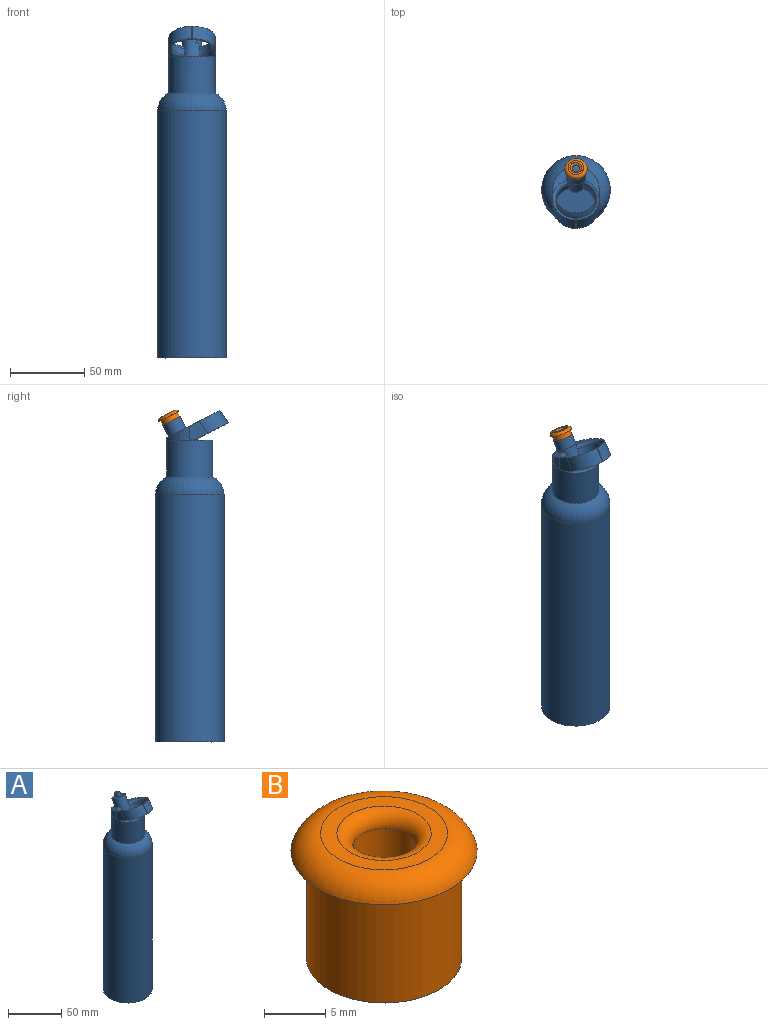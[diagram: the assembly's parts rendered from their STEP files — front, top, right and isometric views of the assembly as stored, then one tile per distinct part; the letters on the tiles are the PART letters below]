
ASSEMBLY  parts=2 mates=1
PART A: 28 faces, bbox 46.8x51.6x225.1 mm
  f0: plane 3.56x1.85mm, normal (0,-0.46,-0.89), area 3.1mm2, adj f2,f8,f24
  f1: plane 30.53x14.5mm, normal (0,-0.46,-0.89), area 25.3mm2, adj f6,f15,f20,f21,f24
  f2: plane 10.81x10.7mm, normal (0,-0.01,-1), area 81.4mm2, adj f0,f8,f10,f18,f22,f24
  f3: cylinder r=13.31mm len=26.62mm, axis (0,0.46,0.89), area 362.6mm2, adj f22,f24,f25
  f4: plane 2.04x1.94mm, normal (0,1,0), area 1.3mm2, adj f5,f9,f17,f19
  f5: plane 31.13x21.03mm, normal (0,0.46,0.89), area 178.6mm2, adj f4,f6,f8,f17,f18,f19,f22,f25
  f6: plane 13.61x12.89mm, normal (1,0,0), area 113.2mm2, adj f1,f5,f7,f14,f19,f21,f24,f25
  f7: plane 19.47x15.6mm, normal (0,-0.01,-1), area 85.2mm2, adj f6,f9,f10,f14,f19,f22,f24
  f8: plane 13.03x12.68mm, normal (-1,0,0), area 102.7mm2, adj f0,f2,f5,f18,f20,f24,f25
  f9: cylinder r=15.56mm len=31.12mm, axis (0,0,-1), area 2432mm2, adj f4,f7,f10,f13,f16,f17
  f10: plane 31.12x22.48mm, normal (0,0,1), area 496.2mm2, adj f2,f7,f9,f16,f22
  f11: cylinder r=22.99mm len=166.25mm, axis (0,0,-1), area 24011.4mm2, adj f12,f13
  f12: plane 45.97x45.97mm, normal (0,0,-1), area 1660mm2, adj f11
  f13: torus R=10.29mm, axis (0,0,1), area 1859.7mm2, adj f9,f11
  f14: plane 6.29x3.27mm, normal (0,-0.46,-0.89), area 6.1mm2, adj f6,f7,f24
  f15: plane 8.24x5.76mm, normal (0,-0.82,0.57), area 5.6mm2, adj f1,f20,f21,f25
  f16: plane 13.94x8.64mm, normal (0,0.01,1), area 0.7mm2, adj f9,f10,f17
  f17: cylinder r=15.58mm len=13.87mm, axis (0,-0.01,-1), area 50.5mm2, adj f4,f5,f9,f16,f18
  f18: extruded ~9.4x7.01mm, area 54.4mm2, adj f2,f5,f8,f17
  f19: cylinder r=15.48mm len=15.38mm, axis (0,-0.01,-1), area 94.5mm2, adj f4,f5,f6,f7
  f20: cylinder r=15.24mm len=19.38mm, axis (0,-0.57,-0.82), area 243.3mm2, adj f1,f8,f15,f24,f25
  f21: cylinder r=15.24mm len=19.42mm, axis (0,0.57,0.82), area 241mm2, adj f1,f6,f15,f25
  f22: cylinder r=6.59mm len=21.88mm, axis (0,-0.46,-0.89), area 457.8mm2, adj f2,f3,f5,f7,f10,f23,f24,f25
  f23: plane 13.17x11.69mm, normal (0,0.46,0.89), area 116mm2, adj f22,f26
  f24: torus R=15.85mm, axis (0,-0.46,-0.89), area 266.9mm2, adj f0,f1,f2,f3,f6,f7,f8,f14
  f25: torus R=15.85mm, axis (0,0.46,0.89), area 291.1mm2, adj f3,f5,f6,f8,f15,f20,f21,f22
  f26: cylinder r=2.54mm len=6.38mm, axis (0,-0.46,-0.89), area 64.9mm2, adj f23,f27
  f27: plane 5.08x4.51mm, normal (0,0.46,0.89), area 20.3mm2, adj f26
PART B: 7 faces, bbox 16.7x16.7x12.5 mm
  f0: cylinder r=6.35mm len=12.7mm, axis (0,0,-1), area 428.7mm2, adj f1,f3
  f1: plane 12.7x12.7mm, normal (0,0,-1), area 106.4mm2, adj f0,f5
  f2: plane 10.39x10.39mm, normal (0,0,1), area 38mm2, adj f4,f6
  f3: plane 15.24x15.24mm, normal (0,0,-1), area 55.7mm2, adj f0,f4
  f4: torus R=5.2mm, axis (0,0,-1), area 133.4mm2, adj f2,f3
  f5: cylinder r=2.54mm len=11.2mm, axis (0,0,1), area 178.8mm2, adj f1,f6
  f6: torus R=3.86mm, axis (0,0,1), area 39.4mm2, adj f2,f5
PLACE A t=(103.02,-24.33,-156.96)mm
PLACE B rot(axis=(-1,0,0),27.5deg) t=(103.02,-15.25,52.15)mm
MATE slider B.f0 <-> A.f26  axis (0,0.46,0.89) through (103.02,-10.08,62.09)mm
